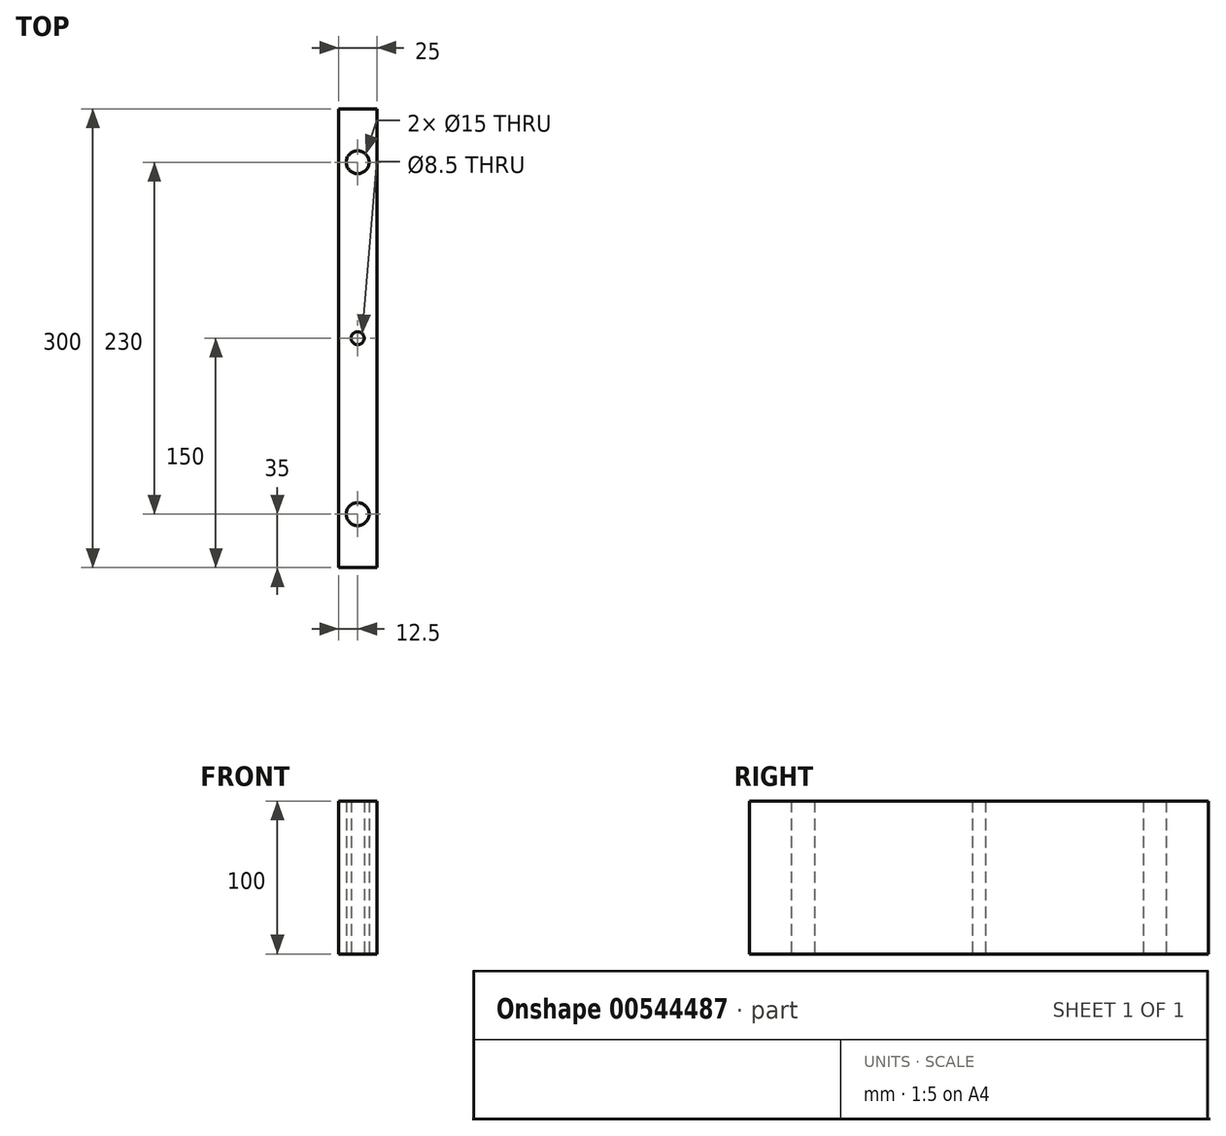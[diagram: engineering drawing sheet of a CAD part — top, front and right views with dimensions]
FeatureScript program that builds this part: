
annotation { "Feature Type Name" : "Feature", "Feature Type Description" : "" }
export const myFeature = defineFeature(function(context is Context, id is Id, definition is map)
    precondition{}
    {
        {
            var Q0;
            Q0=qCreatedBy(makeId("Top.planeOp"),FACE);
            var sketch = newSketch(context, id + "F0", { "sketchPlane" : qUnion([Q0])});
            skLineSegment(sketch, "E0.bottom", {"start": v(-12.5, 150) * mm, "end": v(12.5, 150) * mm});
            skLineSegment(sketch, "E0.top", {"start": v(-12.5, -150) * mm, "end": v(12.5, -150) * mm});
            skLineSegment(sketch, "E0.left", {"start": v(-12.5, 150) * mm, "end": v(-12.5, -150) * mm});
            skLineSegment(sketch, "E0.right", {"start": v(12.5, 150) * mm, "end": v(12.5, -150) * mm});
            skPoint(sketch, "E0.middle", {"position": v(0, 0) * mm});
            skCircle(sketch, "E1", {"center": v(0, 115) * mm, "radius": 7.5 * mm});
            skCircle(sketch, "E2", {"center": v(0, -115) * mm, "radius": 7.5 * mm});
            skLineSegment(sketch, "E3", {"start": v(0, 115) * mm, "end": v(0, -115) * mm, "construction": true});
            skCircle(sketch, "E4", {"center": v(0, 0) * mm, "radius": 4.25 * mm});
            skSolve(sketch);
        }
        {
            var Q0;
            Q0=makeQuery(id+"F0.imprint","IMPRINT",FACE,{"disambiguationData":[TD([[makeQuery(id+"F0.imprint","IMPRINT",EDGE,{"derivedFrom":sQuery(id+"F0.wireOp",EDGE,"E0.bottom")}),-1.0]])]});
            extrude(context, id + "F1", {"entities" : qUnion([Q0]), "endBound" : BoundingType.SYMMETRIC, "depth" : 100 * mm, "offsetDistance" : 25 * mm});
        }
    });
